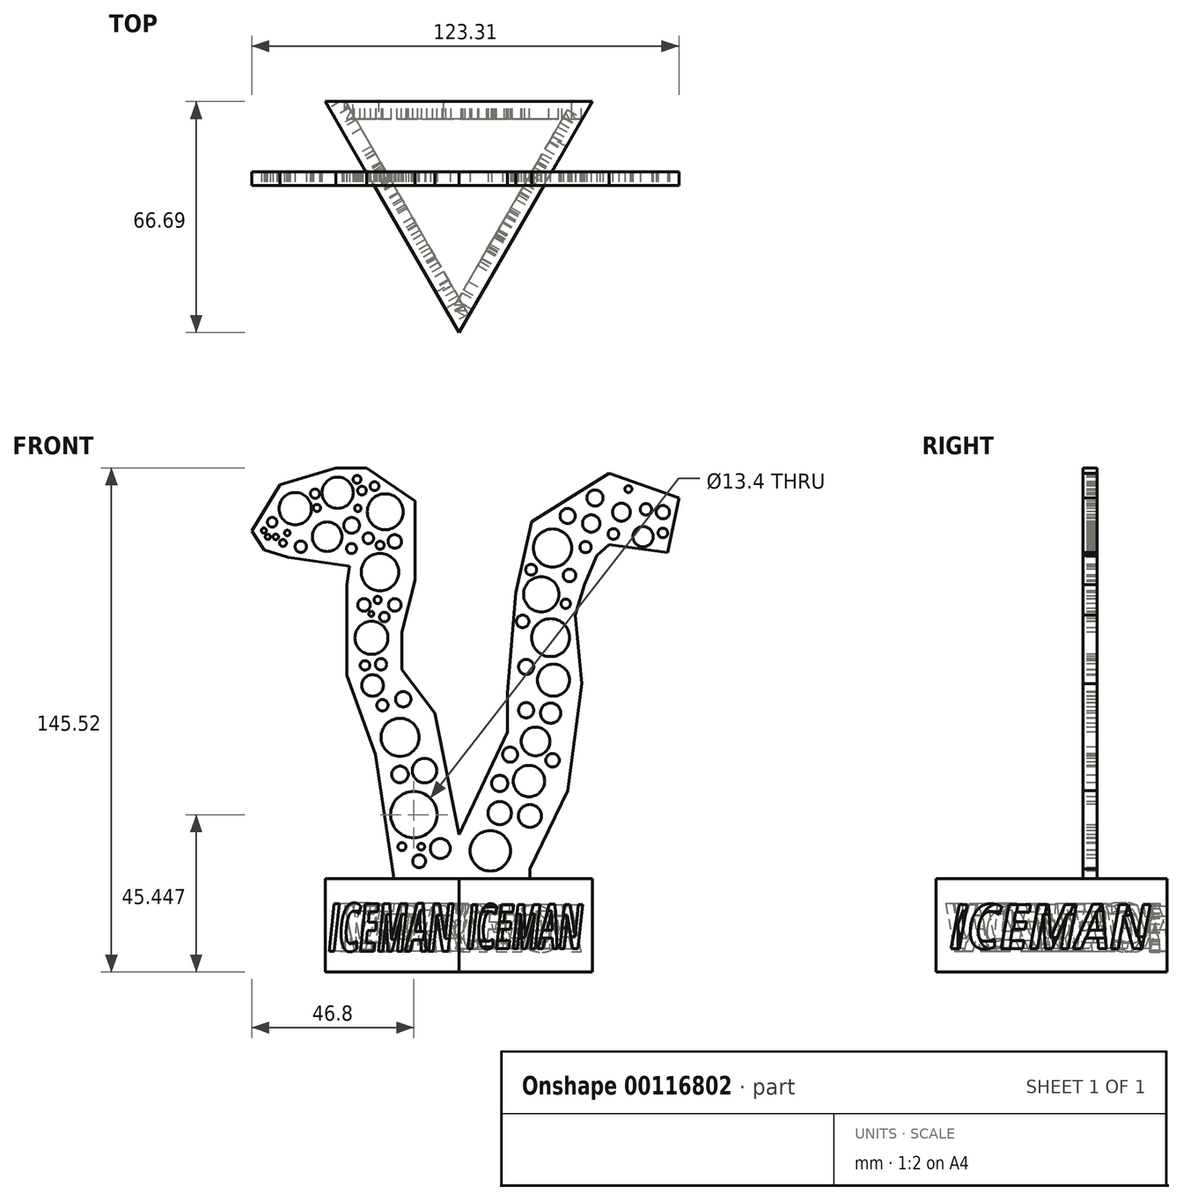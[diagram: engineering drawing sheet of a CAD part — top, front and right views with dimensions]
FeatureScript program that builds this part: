
annotation { "Feature Type Name" : "Feature", "Feature Type Description" : "" }
export const myFeature = defineFeature(function(context is Context, id is Id, definition is map)
    precondition{}
    {
        {
            var Q0;
            Q0=qCreatedBy(makeId("Top.planeOp"),FACE);
            var sketch = newSketch(context, id + "F0", { "sketchPlane" : qUnion([Q0])});
            skCircle(sketch, "E0.cCircle", {"center": v(0, 0) * mm, "radius": 22.23 * mm, "construction": true});
            skLineSegment(sketch, "E0.0", {"start": v(-38.5, 22.23) * mm, "end": v(38.5, 22.23) * mm});
            skLineSegment(sketch, "E0.1", {"start": v(38.5, 22.23) * mm, "end": v(0, -44.46) * mm});
            skLineSegment(sketch, "E0.2", {"start": v(0, -44.46) * mm, "end": v(-38.5, 22.23) * mm});
            skPoint(sketch, "E0.0.midPoint", {"position": v(0, 22.23) * mm});
            skSolve(sketch);
        }
        {
            var Q0;
            Q0=qSketchRegion(id+"F0",true);
            extrude(context, id + "F1", {"entities" : qUnion([Q0]), "depth" : 27 * mm});
        }
        {
            var Q0;
            Q0=makeQuery(id+"F1.opExtrude","SWEPT_FACE",FACE,{"disambiguationData":[OSD([sQuery(id+"F0.wireOp",EDGE,"E0.0")])]});
            var sketch = newSketch(context, id + "F2", { "sketchPlane" : qUnion([Q0])});
            skText(sketch, "E1", { "text": "ICEMAN", "fontName": "OpenSans-BoldItalic.ttf"});
            skLineSegment(sketch, "E2", {"start": v(0, 35.53) * mm, "end": v(0, -12.2) * mm, "construction": true});
            skPoint(sketch, "E2.endSnap0", {"position": v(0, 27) * mm});
            const initialGuessF2  = {"E1": [-0.03582, 0.00594, 1, 0, 0.01323]};
            skSetInitialGuess(sketch, initialGuessF2);
            skSolve(sketch);
        }
        {
            var Q0;
            Q0=qSketchRegion(id+"F2",true);
            extrude(context, id + "F3", {"entities" : qUnion([Q0]), "operationType" : NewBodyOperationType.REMOVE, "oppositeDirection" : true, "depth" : 5 * mm});
        }
        {
            var Q0;
            Q0=makeQuery(id+"F1.opExtrude","SWEPT_FACE",FACE,{"disambiguationData":[OSD([sQuery(id+"F0.wireOp",EDGE,"E0.1")])]});
            var sketch = newSketch(context, id + "F4", { "sketchPlane" : qUnion([Q0])});
            skText(sketch, "E3", { "text": "ICEMAN", "fontName": "OpenSans-BoldItalic.ttf"});
            const initialGuessF4  = {"E3": [-0.0339, 0.0068, 1, 0, 0.01285]};
            skSetInitialGuess(sketch, initialGuessF4);
            skSolve(sketch);
        }
        {
            var Q0;
            Q0=qSketchRegion(id+"F4",true);
            extrude(context, id + "F5", {"entities" : qUnion([Q0]), "operationType" : NewBodyOperationType.REMOVE, "oppositeDirection" : true, "depth" : 5 * mm});
        }
        {
            var Q0;
            Q0=makeQuery(id+"F1.opExtrude","SWEPT_FACE",FACE,{"disambiguationData":[OSD([sQuery(id+"F0.wireOp",EDGE,"E0.2")])]});
            var sketch = newSketch(context, id + "F6", { "sketchPlane" : qUnion([Q0])});
            skText(sketch, "E4", { "text": "ICEMAN", "fontName": "OpenSans-BoldItalic.ttf"});
            const initialGuessF6  = {"E4": [-0.03687, 0.00604, 1, 0, 0.01387]};
            skSetInitialGuess(sketch, initialGuessF6);
            skSolve(sketch);
        }
        {
            var Q0;
            Q0=qSketchRegion(id+"F6",true);
            var Q1;
            Q1=qConstructionFilter(qBodyType(qCreatedBy(id+"F6",EDGE),BodyType.WIRE),ConstructionObject.NO);
            extrude(context, id + "F7", {"entities" : qUnion([Q0]), "operationType" : NewBodyOperationType.REMOVE, "surfaceEntities" : qUnion([Q1]), "oppositeDirection" : true, "depth" : 5 * mm});
        }
        {
            var Q0;
            Q0=makeQuery(id+"F1.opExtrude","CAP_FACE",FACE,{"disambiguationData":[OSD([sQuery(id+"F0.wireOp",EDGE,"E0.0"),sQuery(id+"F0.wireOp",EDGE,"E0.1"),sQuery(id+"F0.wireOp",EDGE,"E0.2")])],"isStart":false});
            var sketch = newSketch(context, id + "F8", { "sketchPlane" : qUnion([Q0])});
            skLineSegment(sketch, "E5.bottom", {"start": v(63.5, 2) * mm, "end": v(-63.5, 2) * mm});
            skLineSegment(sketch, "E5.top", {"start": v(63.5, -2) * mm, "end": v(-63.5, -2) * mm});
            skLineSegment(sketch, "E5.left", {"start": v(63.5, 2) * mm, "end": v(63.5, -2) * mm});
            skLineSegment(sketch, "E5.right", {"start": v(-63.5, 2) * mm, "end": v(-63.5, -2) * mm});
            skPoint(sketch, "E5.middle", {"position": v(0, 0) * mm});
            skSolve(sketch);
        }
        {
            var Q0;
            {var subQ0=sQuery(id+"F8.wireOp",EDGE,"E5.bottom");var subQ1=makeQuery(id+"F1.opExtrude","CAP_EDGE",EDGE,{"disambiguationData":[OSD([sQuery(id+"F0.wireOp",EDGE,"E0.1")])],"isStart":false});var subQ2=makeQuery(id+"F8.imprint","INTERSECT",VERTEX,{"derivedFrom":[subQ1,subQ0]});Q0=makeQuery(id+"F8.imprint","IMPRINT",FACE,{"disambiguationData":[TD([[makeQuery(id+"F8.imprint","IMPRINT",EDGE,{"disambiguationData":[TD([[subQ2,-1.0]])],"derivedFrom":subQ0}),1.0]])]});}
            var Q1;
            {var subQ0=sQuery(id+"F8.wireOp",EDGE,"E5.right");Q1=makeQuery(id+"F8.imprint","IMPRINT",FACE,{"disambiguationData":[TD([[makeQuery(id+"F8.imprint","IMPRINT",EDGE,{"derivedFrom":subQ0}),1.0]])]});}
            var Q2;
            {var subQ0=sQuery(id+"F8.wireOp",EDGE,"E5.left");Q2=makeQuery(id+"F8.imprint","IMPRINT",FACE,{"disambiguationData":[TD([[makeQuery(id+"F8.imprint","IMPRINT",EDGE,{"derivedFrom":subQ0}),-1.0]])]});}
            extrude(context, id + "F9", {"entities" : qUnion([Q0, Q1, Q2]), "operationType" : NewBodyOperationType.ADD, "depth" : 127 * mm});
        }
        {
            var Q0;
            Q0=makeQuery(id+"F9.opExtrude","SWEPT_FACE",FACE,{"disambiguationData":[OSD([sQuery(id+"F8.wireOp",EDGE,"E5.top")])]});
            var sketch = newSketch(context, id + "F10", { "sketchPlane" : qUnion([Q0])});
            skCircle(sketch, "E6", {"center": v(-50.78, 123.83) * mm, "radius": 1 * mm});
            skCircle(sketch, "E7", {"center": v(48.93, 139.4) * mm, "radius": 1 * mm});
            skCircle(sketch, "E8", {"center": v(-47.23, 133.75) * mm, "radius": 4.66 * mm});
            skCircle(sketch, "E9", {"center": v(-35, 138.33) * mm, "radius": 4.51 * mm});
            skCircle(sketch, "E10", {"center": v(-21.26, 132.83) * mm, "radius": 5.2 * mm});
            skCircle(sketch, "E11", {"center": v(-22.79, 115.42) * mm, "radius": 5.4 * mm});
            skCircle(sketch, "E12", {"center": v(-25.23, 96.47) * mm, "radius": 4.77 * mm});
            skCircle(sketch, "E13", {"center": v(-16.98, 67.75) * mm, "radius": 5.5 * mm});
            skCircle(sketch, "E14", {"center": v(-13.01, 45.45) * mm, "radius": 6.7 * mm});
            skCircle(sketch, "E15", {"center": v(-5.37, 35.67) * mm, "radius": 2.88 * mm});
            skCircle(sketch, "E16", {"center": v(-11.48, 32) * mm, "radius": 1.86 * mm});
            skCircle(sketch, "E17", {"center": v(-16.98, 57.06) * mm, "radius": 2.39 * mm});
            skCircle(sketch, "E18", {"center": v(-16.07, 78.75) * mm, "radius": 2.22 * mm});
            skCircle(sketch, "E19", {"center": v(-24.93, 82.72) * mm, "radius": 3.12 * mm});
            skCircle(sketch, "E20", {"center": v(-27.37, 105.95) * mm, "radius": 1.83 * mm});
            skCircle(sketch, "E21", {"center": v(-18.51, 105.95) * mm, "radius": 1.83 * mm});
            skCircle(sketch, "E22", {"center": v(-22.48, 88.83) * mm, "radius": 1.65 * mm});
            skCircle(sketch, "E23", {"center": v(-26.15, 125.2) * mm, "radius": 1.56 * mm});
            skCircle(sketch, "E24", {"center": v(-18.51, 124.28) * mm, "radius": 1.96 * mm});
            skCircle(sketch, "E25", {"center": v(-27.98, 138.94) * mm, "radius": 1.26 * mm});
            skCircle(sketch, "E26", {"center": v(-29.16, 133.83) * mm, "radius": 0.94 * mm});
            skCircle(sketch, "E27", {"center": v(-40.95, 133.95) * mm, "radius": 1.04 * mm});
            skCircle(sketch, "E28", {"center": v(-41.52, 138.07) * mm, "radius": 1.34 * mm});
            skCircle(sketch, "E29", {"center": v(-53.89, 129.83) * mm, "radius": 1.4 * mm});
            skCircle(sketch, "E30", {"center": v(-49.54, 126.74) * mm, "radius": 0.8 * mm});
            skCircle(sketch, "E31", {"center": v(-55.14, 125.6) * mm, "radius": 0.77 * mm});
            skCircle(sketch, "E32", {"center": v(-52.86, 125.6) * mm, "radius": 0.8 * mm});
            skCircle(sketch, "E33", {"center": v(-56.29, 127.42) * mm, "radius": 0.73 * mm});
            skCircle(sketch, "E34", {"center": v(-24.36, 140.24) * mm, "radius": 1.28 * mm});
            skCircle(sketch, "E35", {"center": v(-29.4, 142.19) * mm, "radius": 1.14 * mm});
            skCircle(sketch, "E36", {"center": v(-22.76, 123.19) * mm, "radius": 1.18 * mm});
            skCircle(sketch, "E37", {"center": v(-23.44, 107.4) * mm, "radius": 1.06 * mm});
            skCircle(sketch, "E38", {"center": v(-21.5, 102.47) * mm, "radius": 1.4 * mm});
            skCircle(sketch, "E39", {"center": v(-25.27, 103.39) * mm, "radius": 0.73 * mm});
            skCircle(sketch, "E40", {"center": v(-27.1, 88.5) * mm, "radius": 1.38 * mm});
            skCircle(sketch, "E41", {"center": v(-22.07, 77.01) * mm, "radius": 1.63 * mm});
            skCircle(sketch, "E42", {"center": v(-9.9, 58.14) * mm, "radius": 3.54 * mm});
            skCircle(sketch, "E43", {"center": v(-16.45, 36.2) * mm, "radius": 1.15 * mm});
            skCircle(sketch, "E44", {"center": v(-10.86, 36.2) * mm, "radius": 0.98 * mm});
            skCircle(sketch, "E45", {"center": v(9.06, 35) * mm, "radius": 5.82 * mm});
            skCircle(sketch, "E46", {"center": v(11.79, 45.89) * mm, "radius": 3.37 * mm});
            skCircle(sketch, "E47", {"center": v(20.5, 45.07) * mm, "radius": 3.31 * mm});
            skCircle(sketch, "E48", {"center": v(20.22, 55.14) * mm, "radius": 4.53 * mm});
            skCircle(sketch, "E49", {"center": v(22.13, 66.58) * mm, "radius": 4.15 * mm});
            skCircle(sketch, "E50", {"center": v(26.49, 74.74) * mm, "radius": 2.93 * mm});
            skCircle(sketch, "E51", {"center": v(27.3, 84.27) * mm, "radius": 4.64 * mm});
            skCircle(sketch, "E52", {"center": v(26.49, 96.52) * mm, "radius": 5.47 * mm});
            skCircle(sketch, "E53", {"center": v(19.4, 75.56) * mm, "radius": 2.2 * mm});
            skCircle(sketch, "E54", {"center": v(19.4, 88.08) * mm, "radius": 2.18 * mm});
            skCircle(sketch, "E55", {"center": v(23.76, 109.04) * mm, "radius": 5.09 * mm});
            skCircle(sketch, "E56", {"center": v(27.03, 122.38) * mm, "radius": 5.51 * mm});
            skCircle(sketch, "E57", {"center": v(38.2, 129.46) * mm, "radius": 2.5 * mm});
            skCircle(sketch, "E58", {"center": v(31.39, 131.64) * mm, "radius": 2.2 * mm});
            skCircle(sketch, "E59", {"center": v(39.28, 136.8) * mm, "radius": 2.34 * mm});
            skCircle(sketch, "E60", {"center": v(46.9, 132.72) * mm, "radius": 2.58 * mm});
            skCircle(sketch, "E61", {"center": v(53.16, 125.65) * mm, "radius": 2.93 * mm});
            skCircle(sketch, "E62", {"center": v(53.98, 133.54) * mm, "radius": 1.66 * mm});
            skCircle(sketch, "E63", {"center": v(58.88, 132.72) * mm, "radius": 1.92 * mm});
            skCircle(sketch, "E64", {"center": v(58.88, 126.74) * mm, "radius": 1.39 * mm});
            skCircle(sketch, "E65", {"center": v(31.93, 114.49) * mm, "radius": 1.83 * mm});
            skCircle(sketch, "E66", {"center": v(30.84, 106.32) * mm, "radius": 1.36 * mm});
            skCircle(sketch, "E67", {"center": v(36.56, 122.65) * mm, "radius": 1.63 * mm});
            skLineSegment(sketch, "E68", {"start": v(0, 39.63) * mm, "end": v(-7, 74.74) * mm});
            skLineSegment(sketch, "E69", {"start": v(-7, 74.74) * mm, "end": v(-16.52, 87.27) * mm});
            skLineSegment(sketch, "E70", {"start": v(-16.52, 87.27) * mm, "end": v(-16.52, 98.15) * mm});
            skLineSegment(sketch, "E71", {"start": v(-16.52, 98.15) * mm, "end": v(-12.71, 113.13) * mm});
            skLineSegment(sketch, "E72", {"start": v(-12.71, 113.13) * mm, "end": v(-12.71, 136) * mm});
            skLineSegment(sketch, "E73", {"start": v(-12.71, 136) * mm, "end": v(-26.6, 145.52) * mm});
            skLineSegment(sketch, "E74", {"start": v(-26.6, 145.52) * mm, "end": v(-35.58, 145.52) * mm});
            skLineSegment(sketch, "E75", {"start": v(-35.58, 145.52) * mm, "end": v(-51.64, 140.62) * mm});
            skLineSegment(sketch, "E76", {"start": v(-51.64, 140.62) * mm, "end": v(-59.8, 127.28) * mm});
            skLineSegment(sketch, "E77", {"start": v(-59.8, 127.28) * mm, "end": v(-56.27, 121.84) * mm});
            skLineSegment(sketch, "E78", {"start": v(-56.27, 121.84) * mm, "end": v(-49.19, 119.66) * mm});
            skLineSegment(sketch, "E79", {"start": v(-31.54, 117.1) * mm, "end": v(-32.31, 111.76) * mm});
            skLineSegment(sketch, "E80", {"start": v(-32.31, 111.76) * mm, "end": v(-32.31, 85.63) * mm});
            skLineSegment(sketch, "E81", {"start": v(-32.31, 85.63) * mm, "end": v(-24.15, 62.77) * mm});
            skLineSegment(sketch, "E82", {"start": v(-24.15, 62.77) * mm, "end": v(-18.7, 27) * mm});
            skLineSegment(sketch, "E83", {"start": v(0, 39.63) * mm, "end": v(14.01, 69.28) * mm});
            skLineSegment(sketch, "E84", {"start": v(14.01, 69.28) * mm, "end": v(14.01, 80.73) * mm});
            skLineSegment(sketch, "E85", {"start": v(14.01, 80.73) * mm, "end": v(16.41, 109.59) * mm});
            skLineSegment(sketch, "E86", {"start": v(16.41, 109.59) * mm, "end": v(21.04, 130) * mm});
            skLineSegment(sketch, "E87", {"start": v(21.04, 130) * mm, "end": v(43.36, 143.89) * mm});
            skLineSegment(sketch, "E88", {"start": v(43.36, 143.89) * mm, "end": v(63.5, 136.8) * mm});
            skLineSegment(sketch, "E89", {"start": v(63.5, 136.8) * mm, "end": v(60.24, 121.02) * mm});
            skLineSegment(sketch, "E90", {"start": v(60.24, 121.02) * mm, "end": v(43.34, 123.36) * mm});
            skLineSegment(sketch, "E91", {"start": v(43.34, 123.36) * mm, "end": v(39.82, 120.2) * mm});
            skLineSegment(sketch, "E92", {"start": v(39.82, 120.2) * mm, "end": v(36.29, 111.76) * mm});
            skLineSegment(sketch, "E93", {"start": v(36.29, 111.76) * mm, "end": v(33.56, 103.05) * mm});
            skLineSegment(sketch, "E94", {"start": v(33.56, 103.05) * mm, "end": v(35.47, 83.18) * mm});
            skLineSegment(sketch, "E95", {"start": v(35.47, 83.18) * mm, "end": v(31.39, 52.42) * mm});
            skLineSegment(sketch, "E96", {"start": v(31.39, 52.42) * mm, "end": v(20.5, 29.83) * mm});
            skCircle(sketch, "E97", {"center": v(11.79, 54.45) * mm, "radius": 2.34 * mm});
            skPoint(sketch, "E97.centerSnap0", {"position": v(7, 54.45) * mm});
            skCircle(sketch, "E98", {"center": v(14.78, 62.77) * mm, "radius": 2.18 * mm});
            skCircle(sketch, "E99", {"center": v(27.03, 61.13) * mm, "radius": 1.96 * mm});
            skLineSegment(sketch, "E100", {"start": v(-49.19, 119.66) * mm, "end": v(-31.54, 117.1) * mm});
            skCircle(sketch, "E101", {"center": v(-38.03, 125.65) * mm, "radius": 4.26 * mm});
            skCircle(sketch, "E102", {"center": v(-30.95, 128.91) * mm, "radius": 2.27 * mm});
            skCircle(sketch, "E103", {"center": v(-31, 122.23) * mm, "radius": 1.45 * mm});
            skCircle(sketch, "E104", {"center": v(-45.63, 122.77) * mm, "radius": 1.65 * mm});
            skCircle(sketch, "E105", {"center": v(20.84, 116.12) * mm, "radius": 1.58 * mm});
            skCircle(sketch, "E106", {"center": v(18.41, 101.2) * mm, "radius": 1.82 * mm});
            skCircle(sketch, "E107", {"center": v(44.6, 126.43) * mm, "radius": 1.53 * mm});
            skLineSegment(sketch, "E108", {"start": v(20.5, 29.83) * mm, "end": v(20.5, 27) * mm});
            skPoint(sketch, "E108.endSnap0", {"position": v(0, 27) * mm});
            skSolve(sketch);
        }
        {
            var Q0;
            Q0=makeQuery(id+"F10.imprint","IMPRINT",FACE,{"disambiguationData":[TD([[makeQuery(id+"F10.imprint","IMPRINT",EDGE,{"derivedFrom":sQuery(id+"F10.wireOp",EDGE,"E68")}),-1.0]])]});
            var Q1;
            {var subQ13=sQuery(id+"F10.wireOp",EDGE,"E89");Q1=makeQuery(id+"F10.imprint","IMPRINT",FACE,{"disambiguationData":[TD([[makeQuery(id+"F10.imprint","IMPRINT",EDGE,{"derivedFrom":subQ13}),1.0]])]});}
            var Q2;
            Q2=makeQuery(id+"F10.imprint","IMPRINT",FACE,{"disambiguationData":[TD([[makeQuery(id+"F10.imprint","IMPRINT",EDGE,{"derivedFrom":sQuery(id+"F10.wireOp",EDGE,"E101")}),1.0]])]});
            var Q3;
            Q3=makeQuery(id+"F10.imprint","IMPRINT",FACE,{"disambiguationData":[TD([[makeQuery(id+"F10.imprint","IMPRINT",EDGE,{"derivedFrom":sQuery(id+"F10.wireOp",EDGE,"E11")}),1.0]])]});
            var Q4;
            Q4=makeQuery(id+"F10.imprint","IMPRINT",FACE,{"disambiguationData":[TD([[makeQuery(id+"F10.imprint","IMPRINT",EDGE,{"derivedFrom":sQuery(id+"F10.wireOp",EDGE,"E9")}),1.0]])]});
            var Q5;
            Q5=makeQuery(id+"F10.imprint","IMPRINT",FACE,{"disambiguationData":[TD([[makeQuery(id+"F10.imprint","IMPRINT",EDGE,{"derivedFrom":sQuery(id+"F10.wireOp",EDGE,"E8")}),1.0]])]});
            var Q6;
            Q6=makeQuery(id+"F10.imprint","IMPRINT",FACE,{"disambiguationData":[TD([[makeQuery(id+"F10.imprint","IMPRINT",EDGE,{"derivedFrom":sQuery(id+"F10.wireOp",EDGE,"E29")}),1.0]])]});
            var Q7;
            Q7=makeQuery(id+"F10.imprint","IMPRINT",FACE,{"disambiguationData":[TD([[makeQuery(id+"F10.imprint","IMPRINT",EDGE,{"derivedFrom":sQuery(id+"F10.wireOp",EDGE,"E33")}),1.0]])]});
            var Q8;
            Q8=makeQuery(id+"F10.imprint","IMPRINT",FACE,{"disambiguationData":[TD([[makeQuery(id+"F10.imprint","IMPRINT",EDGE,{"derivedFrom":sQuery(id+"F10.wireOp",EDGE,"E31")}),1.0]])]});
            var Q9;
            Q9=makeQuery(id+"F10.imprint","IMPRINT",FACE,{"disambiguationData":[TD([[makeQuery(id+"F10.imprint","IMPRINT",EDGE,{"derivedFrom":sQuery(id+"F10.wireOp",EDGE,"E32")}),1.0]])]});
            var Q10;
            Q10=makeQuery(id+"F10.imprint","IMPRINT",FACE,{"disambiguationData":[TD([[makeQuery(id+"F10.imprint","IMPRINT",EDGE,{"derivedFrom":sQuery(id+"F10.wireOp",EDGE,"E6")}),1.0]])]});
            var Q11;
            Q11=makeQuery(id+"F10.imprint","IMPRINT",FACE,{"disambiguationData":[TD([[makeQuery(id+"F10.imprint","IMPRINT",EDGE,{"derivedFrom":sQuery(id+"F10.wireOp",EDGE,"E30")}),1.0]])]});
            var Q12;
            Q12=makeQuery(id+"F10.imprint","IMPRINT",FACE,{"disambiguationData":[TD([[makeQuery(id+"F10.imprint","IMPRINT",EDGE,{"derivedFrom":sQuery(id+"F10.wireOp",EDGE,"E104")}),1.0]])]});
            var Q13;
            Q13=makeQuery(id+"F10.imprint","IMPRINT",FACE,{"disambiguationData":[TD([[makeQuery(id+"F10.imprint","IMPRINT",EDGE,{"derivedFrom":sQuery(id+"F10.wireOp",EDGE,"E102")}),1.0]])]});
            var Q14;
            Q14=makeQuery(id+"F10.imprint","IMPRINT",FACE,{"disambiguationData":[TD([[makeQuery(id+"F10.imprint","IMPRINT",EDGE,{"derivedFrom":sQuery(id+"F10.wireOp",EDGE,"E27")}),1.0]])]});
            var Q15;
            Q15=makeQuery(id+"F10.imprint","IMPRINT",FACE,{"disambiguationData":[TD([[makeQuery(id+"F10.imprint","IMPRINT",EDGE,{"derivedFrom":sQuery(id+"F10.wireOp",EDGE,"E28")}),1.0]])]});
            var Q16;
            Q16=makeQuery(id+"F10.imprint","IMPRINT",FACE,{"disambiguationData":[TD([[makeQuery(id+"F10.imprint","IMPRINT",EDGE,{"derivedFrom":sQuery(id+"F10.wireOp",EDGE,"E10")}),1.0]])]});
            var Q17;
            Q17=makeQuery(id+"F10.imprint","IMPRINT",FACE,{"disambiguationData":[TD([[makeQuery(id+"F10.imprint","IMPRINT",EDGE,{"derivedFrom":sQuery(id+"F10.wireOp",EDGE,"E26")}),1.0]])]});
            var Q18;
            Q18=makeQuery(id+"F10.imprint","IMPRINT",FACE,{"disambiguationData":[TD([[makeQuery(id+"F10.imprint","IMPRINT",EDGE,{"derivedFrom":sQuery(id+"F10.wireOp",EDGE,"E23")}),1.0]])]});
            var Q19;
            Q19=makeQuery(id+"F10.imprint","IMPRINT",FACE,{"disambiguationData":[TD([[makeQuery(id+"F10.imprint","IMPRINT",EDGE,{"derivedFrom":sQuery(id+"F10.wireOp",EDGE,"E103")}),1.0]])]});
            var Q20;
            Q20=makeQuery(id+"F10.imprint","IMPRINT",FACE,{"disambiguationData":[TD([[makeQuery(id+"F10.imprint","IMPRINT",EDGE,{"derivedFrom":sQuery(id+"F10.wireOp",EDGE,"E36")}),1.0]])]});
            var Q21;
            Q21=makeQuery(id+"F10.imprint","IMPRINT",FACE,{"disambiguationData":[TD([[makeQuery(id+"F10.imprint","IMPRINT",EDGE,{"derivedFrom":sQuery(id+"F10.wireOp",EDGE,"E24")}),1.0]])]});
            var Q22;
            Q22=makeQuery(id+"F10.imprint","IMPRINT",FACE,{"disambiguationData":[TD([[makeQuery(id+"F10.imprint","IMPRINT",EDGE,{"derivedFrom":sQuery(id+"F10.wireOp",EDGE,"E37")}),1.0]])]});
            var Q23;
            Q23=makeQuery(id+"F10.imprint","IMPRINT",FACE,{"disambiguationData":[TD([[makeQuery(id+"F10.imprint","IMPRINT",EDGE,{"derivedFrom":sQuery(id+"F10.wireOp",EDGE,"E20")}),1.0]])]});
            var Q24;
            Q24=makeQuery(id+"F10.imprint","IMPRINT",FACE,{"disambiguationData":[TD([[makeQuery(id+"F10.imprint","IMPRINT",EDGE,{"derivedFrom":sQuery(id+"F10.wireOp",EDGE,"E39")}),1.0]])]});
            var Q25;
            Q25=makeQuery(id+"F10.imprint","IMPRINT",FACE,{"disambiguationData":[TD([[makeQuery(id+"F10.imprint","IMPRINT",EDGE,{"derivedFrom":sQuery(id+"F10.wireOp",EDGE,"E38")}),1.0]])]});
            var Q26;
            Q26=makeQuery(id+"F10.imprint","IMPRINT",FACE,{"disambiguationData":[TD([[makeQuery(id+"F10.imprint","IMPRINT",EDGE,{"derivedFrom":sQuery(id+"F10.wireOp",EDGE,"E21")}),1.0]])]});
            var Q27;
            Q27=makeQuery(id+"F10.imprint","IMPRINT",FACE,{"disambiguationData":[TD([[makeQuery(id+"F10.imprint","IMPRINT",EDGE,{"derivedFrom":sQuery(id+"F10.wireOp",EDGE,"E12")}),1.0]])]});
            var Q28;
            Q28=makeQuery(id+"F10.imprint","IMPRINT",FACE,{"disambiguationData":[TD([[makeQuery(id+"F10.imprint","IMPRINT",EDGE,{"derivedFrom":sQuery(id+"F10.wireOp",EDGE,"E40")}),1.0]])]});
            var Q29;
            Q29=makeQuery(id+"F10.imprint","IMPRINT",FACE,{"disambiguationData":[TD([[makeQuery(id+"F10.imprint","IMPRINT",EDGE,{"derivedFrom":sQuery(id+"F10.wireOp",EDGE,"E22")}),1.0]])]});
            var Q30;
            Q30=makeQuery(id+"F10.imprint","IMPRINT",FACE,{"disambiguationData":[TD([[makeQuery(id+"F10.imprint","IMPRINT",EDGE,{"derivedFrom":sQuery(id+"F10.wireOp",EDGE,"E19")}),1.0]])]});
            var Q31;
            Q31=makeQuery(id+"F10.imprint","IMPRINT",FACE,{"disambiguationData":[TD([[makeQuery(id+"F10.imprint","IMPRINT",EDGE,{"derivedFrom":sQuery(id+"F10.wireOp",EDGE,"E41")}),1.0]])]});
            var Q32;
            Q32=makeQuery(id+"F10.imprint","IMPRINT",FACE,{"disambiguationData":[TD([[makeQuery(id+"F10.imprint","IMPRINT",EDGE,{"derivedFrom":sQuery(id+"F10.wireOp",EDGE,"E18")}),1.0]])]});
            var Q33;
            Q33=makeQuery(id+"F10.imprint","IMPRINT",FACE,{"disambiguationData":[TD([[makeQuery(id+"F10.imprint","IMPRINT",EDGE,{"derivedFrom":sQuery(id+"F10.wireOp",EDGE,"E13")}),1.0]])]});
            var Q34;
            Q34=makeQuery(id+"F10.imprint","IMPRINT",FACE,{"disambiguationData":[TD([[makeQuery(id+"F10.imprint","IMPRINT",EDGE,{"derivedFrom":sQuery(id+"F10.wireOp",EDGE,"E63")}),1.0]])]});
            var Q35;
            Q35=makeQuery(id+"F10.imprint","IMPRINT",FACE,{"disambiguationData":[TD([[makeQuery(id+"F10.imprint","IMPRINT",EDGE,{"derivedFrom":sQuery(id+"F10.wireOp",EDGE,"E60")}),1.0]])]});
            var Q36;
            Q36=makeQuery(id+"F10.imprint","IMPRINT",FACE,{"disambiguationData":[TD([[makeQuery(id+"F10.imprint","IMPRINT",EDGE,{"derivedFrom":sQuery(id+"F10.wireOp",EDGE,"E107")}),1.0]])]});
            var Q37;
            Q37=makeQuery(id+"F10.imprint","IMPRINT",FACE,{"disambiguationData":[TD([[makeQuery(id+"F10.imprint","IMPRINT",EDGE,{"derivedFrom":sQuery(id+"F10.wireOp",EDGE,"E57")}),1.0]])]});
            var Q38;
            Q38=makeQuery(id+"F10.imprint","IMPRINT",FACE,{"disambiguationData":[TD([[makeQuery(id+"F10.imprint","IMPRINT",EDGE,{"derivedFrom":sQuery(id+"F10.wireOp",EDGE,"E58")}),1.0]])]});
            var Q39;
            Q39=makeQuery(id+"F10.imprint","IMPRINT",FACE,{"disambiguationData":[TD([[makeQuery(id+"F10.imprint","IMPRINT",EDGE,{"derivedFrom":sQuery(id+"F10.wireOp",EDGE,"E56")}),1.0]])]});
            var Q40;
            Q40=makeQuery(id+"F10.imprint","IMPRINT",FACE,{"disambiguationData":[TD([[makeQuery(id+"F10.imprint","IMPRINT",EDGE,{"derivedFrom":sQuery(id+"F10.wireOp",EDGE,"E55")}),1.0]])]});
            var Q41;
            Q41=makeQuery(id+"F10.imprint","IMPRINT",FACE,{"disambiguationData":[TD([[makeQuery(id+"F10.imprint","IMPRINT",EDGE,{"derivedFrom":sQuery(id+"F10.wireOp",EDGE,"E105")}),1.0]])]});
            var Q42;
            Q42=makeQuery(id+"F10.imprint","IMPRINT",FACE,{"disambiguationData":[TD([[makeQuery(id+"F10.imprint","IMPRINT",EDGE,{"derivedFrom":sQuery(id+"F10.wireOp",EDGE,"E106")}),1.0]])]});
            var Q43;
            Q43=makeQuery(id+"F10.imprint","IMPRINT",FACE,{"disambiguationData":[TD([[makeQuery(id+"F10.imprint","IMPRINT",EDGE,{"derivedFrom":sQuery(id+"F10.wireOp",EDGE,"E66")}),1.0]])]});
            var Q44;
            Q44=makeQuery(id+"F10.imprint","IMPRINT",FACE,{"disambiguationData":[TD([[makeQuery(id+"F10.imprint","IMPRINT",EDGE,{"derivedFrom":sQuery(id+"F10.wireOp",EDGE,"E65")}),1.0]])]});
            var Q45;
            Q45=makeQuery(id+"F10.imprint","IMPRINT",FACE,{"disambiguationData":[TD([[makeQuery(id+"F10.imprint","IMPRINT",EDGE,{"derivedFrom":sQuery(id+"F10.wireOp",EDGE,"E52")}),1.0]])]});
            var Q46;
            Q46=makeQuery(id+"F10.imprint","IMPRINT",FACE,{"disambiguationData":[TD([[makeQuery(id+"F10.imprint","IMPRINT",EDGE,{"derivedFrom":sQuery(id+"F10.wireOp",EDGE,"E51")}),1.0]])]});
            var Q47;
            Q47=makeQuery(id+"F10.imprint","IMPRINT",FACE,{"disambiguationData":[TD([[makeQuery(id+"F10.imprint","IMPRINT",EDGE,{"derivedFrom":sQuery(id+"F10.wireOp",EDGE,"E54")}),1.0]])]});
            var Q48;
            Q48=makeQuery(id+"F10.imprint","IMPRINT",FACE,{"disambiguationData":[TD([[makeQuery(id+"F10.imprint","IMPRINT",EDGE,{"derivedFrom":sQuery(id+"F10.wireOp",EDGE,"E53")}),1.0]])]});
            var Q49;
            Q49=makeQuery(id+"F10.imprint","IMPRINT",FACE,{"disambiguationData":[TD([[makeQuery(id+"F10.imprint","IMPRINT",EDGE,{"derivedFrom":sQuery(id+"F10.wireOp",EDGE,"E50")}),1.0]])]});
            var Q50;
            Q50=makeQuery(id+"F10.imprint","IMPRINT",FACE,{"disambiguationData":[TD([[makeQuery(id+"F10.imprint","IMPRINT",EDGE,{"derivedFrom":sQuery(id+"F10.wireOp",EDGE,"E49")}),1.0]])]});
            var Q51;
            Q51=makeQuery(id+"F10.imprint","IMPRINT",FACE,{"disambiguationData":[TD([[makeQuery(id+"F10.imprint","IMPRINT",EDGE,{"derivedFrom":sQuery(id+"F10.wireOp",EDGE,"E98")}),1.0]])]});
            var Q52;
            Q52=makeQuery(id+"F10.imprint","IMPRINT",FACE,{"disambiguationData":[TD([[makeQuery(id+"F10.imprint","IMPRINT",EDGE,{"derivedFrom":sQuery(id+"F10.wireOp",EDGE,"E48")}),1.0]])]});
            var Q53;
            Q53=makeQuery(id+"F10.imprint","IMPRINT",FACE,{"disambiguationData":[TD([[makeQuery(id+"F10.imprint","IMPRINT",EDGE,{"derivedFrom":sQuery(id+"F10.wireOp",EDGE,"E99")}),1.0]])]});
            var Q54;
            Q54=makeQuery(id+"F10.imprint","IMPRINT",FACE,{"disambiguationData":[TD([[makeQuery(id+"F10.imprint","IMPRINT",EDGE,{"derivedFrom":sQuery(id+"F10.wireOp",EDGE,"E47")}),1.0]])]});
            var Q55;
            Q55=makeQuery(id+"F10.imprint","IMPRINT",FACE,{"disambiguationData":[TD([[makeQuery(id+"F10.imprint","IMPRINT",EDGE,{"derivedFrom":sQuery(id+"F10.wireOp",EDGE,"E46")}),1.0]])]});
            var Q56;
            Q56=makeQuery(id+"F10.imprint","IMPRINT",FACE,{"disambiguationData":[TD([[makeQuery(id+"F10.imprint","IMPRINT",EDGE,{"derivedFrom":sQuery(id+"F10.wireOp",EDGE,"E97")}),1.0]])]});
            var Q57;
            Q57=makeQuery(id+"F10.imprint","IMPRINT",FACE,{"disambiguationData":[TD([[makeQuery(id+"F10.imprint","IMPRINT",EDGE,{"derivedFrom":sQuery(id+"F10.wireOp",EDGE,"E45")}),1.0]])]});
            var Q58;
            Q58=makeQuery(id+"F10.imprint","IMPRINT",FACE,{"disambiguationData":[TD([[makeQuery(id+"F10.imprint","IMPRINT",EDGE,{"derivedFrom":sQuery(id+"F10.wireOp",EDGE,"E16")}),1.0]])]});
            var Q59;
            Q59=makeQuery(id+"F10.imprint","IMPRINT",FACE,{"disambiguationData":[TD([[makeQuery(id+"F10.imprint","IMPRINT",EDGE,{"derivedFrom":sQuery(id+"F10.wireOp",EDGE,"E15")}),1.0]])]});
            var Q60;
            Q60=makeQuery(id+"F10.imprint","IMPRINT",FACE,{"disambiguationData":[TD([[makeQuery(id+"F10.imprint","IMPRINT",EDGE,{"derivedFrom":sQuery(id+"F10.wireOp",EDGE,"E44")}),1.0]])]});
            var Q61;
            Q61=makeQuery(id+"F10.imprint","IMPRINT",FACE,{"disambiguationData":[TD([[makeQuery(id+"F10.imprint","IMPRINT",EDGE,{"derivedFrom":sQuery(id+"F10.wireOp",EDGE,"E43")}),1.0]])]});
            var Q62;
            Q62=makeQuery(id+"F10.imprint","IMPRINT",FACE,{"disambiguationData":[TD([[makeQuery(id+"F10.imprint","IMPRINT",EDGE,{"derivedFrom":sQuery(id+"F10.wireOp",EDGE,"E14")}),1.0]])]});
            var Q63;
            Q63=makeQuery(id+"F10.imprint","IMPRINT",FACE,{"disambiguationData":[TD([[makeQuery(id+"F10.imprint","IMPRINT",EDGE,{"derivedFrom":sQuery(id+"F10.wireOp",EDGE,"E17")}),1.0]])]});
            var Q64;
            Q64=makeQuery(id+"F10.imprint","IMPRINT",FACE,{"disambiguationData":[TD([[makeQuery(id+"F10.imprint","IMPRINT",EDGE,{"derivedFrom":sQuery(id+"F10.wireOp",EDGE,"E42")}),1.0]])]});
            var Q65;
            Q65=makeQuery(id+"F10.imprint","IMPRINT",FACE,{"disambiguationData":[TD([[makeQuery(id+"F10.imprint","IMPRINT",EDGE,{"derivedFrom":sQuery(id+"F10.wireOp",EDGE,"E59")}),1.0]])]});
            var Q66;
            Q66=makeQuery(id+"F10.imprint","IMPRINT",FACE,{"disambiguationData":[TD([[makeQuery(id+"F10.imprint","IMPRINT",EDGE,{"derivedFrom":sQuery(id+"F10.wireOp",EDGE,"E7")}),1.0]])]});
            var Q67;
            Q67=makeQuery(id+"F10.imprint","IMPRINT",FACE,{"disambiguationData":[TD([[makeQuery(id+"F10.imprint","IMPRINT",EDGE,{"derivedFrom":sQuery(id+"F10.wireOp",EDGE,"E62")}),1.0]])]});
            var Q68;
            Q68=makeQuery(id+"F10.imprint","IMPRINT",FACE,{"disambiguationData":[TD([[makeQuery(id+"F10.imprint","IMPRINT",EDGE,{"derivedFrom":sQuery(id+"F10.wireOp",EDGE,"E61")}),1.0]])]});
            var Q69;
            Q69=makeQuery(id+"F10.imprint","IMPRINT",FACE,{"disambiguationData":[TD([[makeQuery(id+"F10.imprint","IMPRINT",EDGE,{"derivedFrom":sQuery(id+"F10.wireOp",EDGE,"E64")}),1.0]])]});
            var Q70;
            Q70=makeQuery(id+"F10.imprint","IMPRINT",FACE,{"disambiguationData":[TD([[makeQuery(id+"F10.imprint","IMPRINT",EDGE,{"derivedFrom":sQuery(id+"F10.wireOp",EDGE,"E67")}),1.0]])]});
            var Q71;
            Q71=makeQuery(id+"F10.imprint","IMPRINT",FACE,{"disambiguationData":[TD([[makeQuery(id+"F10.imprint","IMPRINT",EDGE,{"derivedFrom":sQuery(id+"F10.wireOp",EDGE,"E35")}),1.0]])]});
            var Q72;
            Q72=makeQuery(id+"F10.imprint","IMPRINT",FACE,{"disambiguationData":[TD([[makeQuery(id+"F10.imprint","IMPRINT",EDGE,{"derivedFrom":sQuery(id+"F10.wireOp",EDGE,"E25")}),1.0]])]});
            var Q73;
            Q73=makeQuery(id+"F10.imprint","IMPRINT",FACE,{"disambiguationData":[TD([[makeQuery(id+"F10.imprint","IMPRINT",EDGE,{"derivedFrom":sQuery(id+"F10.wireOp",EDGE,"E34")}),1.0]])]});
            extrude(context, id + "F11", {"entities" : qUnion([Q0, Q1, Q2, Q3, Q4, Q5, Q6, Q7, Q8, Q9, Q10, Q11, Q12, Q13, Q14, Q15, Q16, Q17, Q18, Q19, Q20, Q21, Q22, Q23, Q24, Q25, Q26, Q27, Q28, Q29, Q30, Q31, Q32, Q33, Q34, Q35, Q36, Q37, Q38, Q39, Q40, Q41, Q42, Q43, Q44, Q45, Q46, Q47, Q48, Q49, Q50, Q51, Q52, Q53, Q54, Q55, Q56, Q57, Q58, Q59, Q60, Q61, Q62, Q63, Q64, Q65, Q66, Q67, Q68, Q69, Q70, Q71, Q72, Q73]), "operationType" : NewBodyOperationType.REMOVE, "endBound" : BoundingType.THROUGH_ALL, "oppositeDirection" : true, "depth" : 25 * mm});
        }
    });
